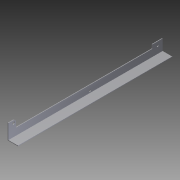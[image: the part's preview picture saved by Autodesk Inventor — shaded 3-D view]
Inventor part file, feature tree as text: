
AUTODESK INVENTOR PART (.ipt)
format: ipt  version: 2012 (Build 160160000, 160)  size: 91,136 bytes
history: native  units: in
note: dims shown in document units (in); Inventor stores cm internally (conversion verified against a paired STEP export)
features: other x3, sketch x1
ambient origin geometry x8: Origin, YZ Plane, XZ Plane, XY Plane, X Axis, Y Axis, Z Axis, Center Point
bodies: Solid1 (feature_tree)
feature tree (4):
  other  "8 ball top roller L frame.ipt"
  other  "Solid1::8 ball top roller L frame.ipt"
  sketch  "Sketch1"  dims[d0=0.3937in]
  other  "TaggingFeature1"
